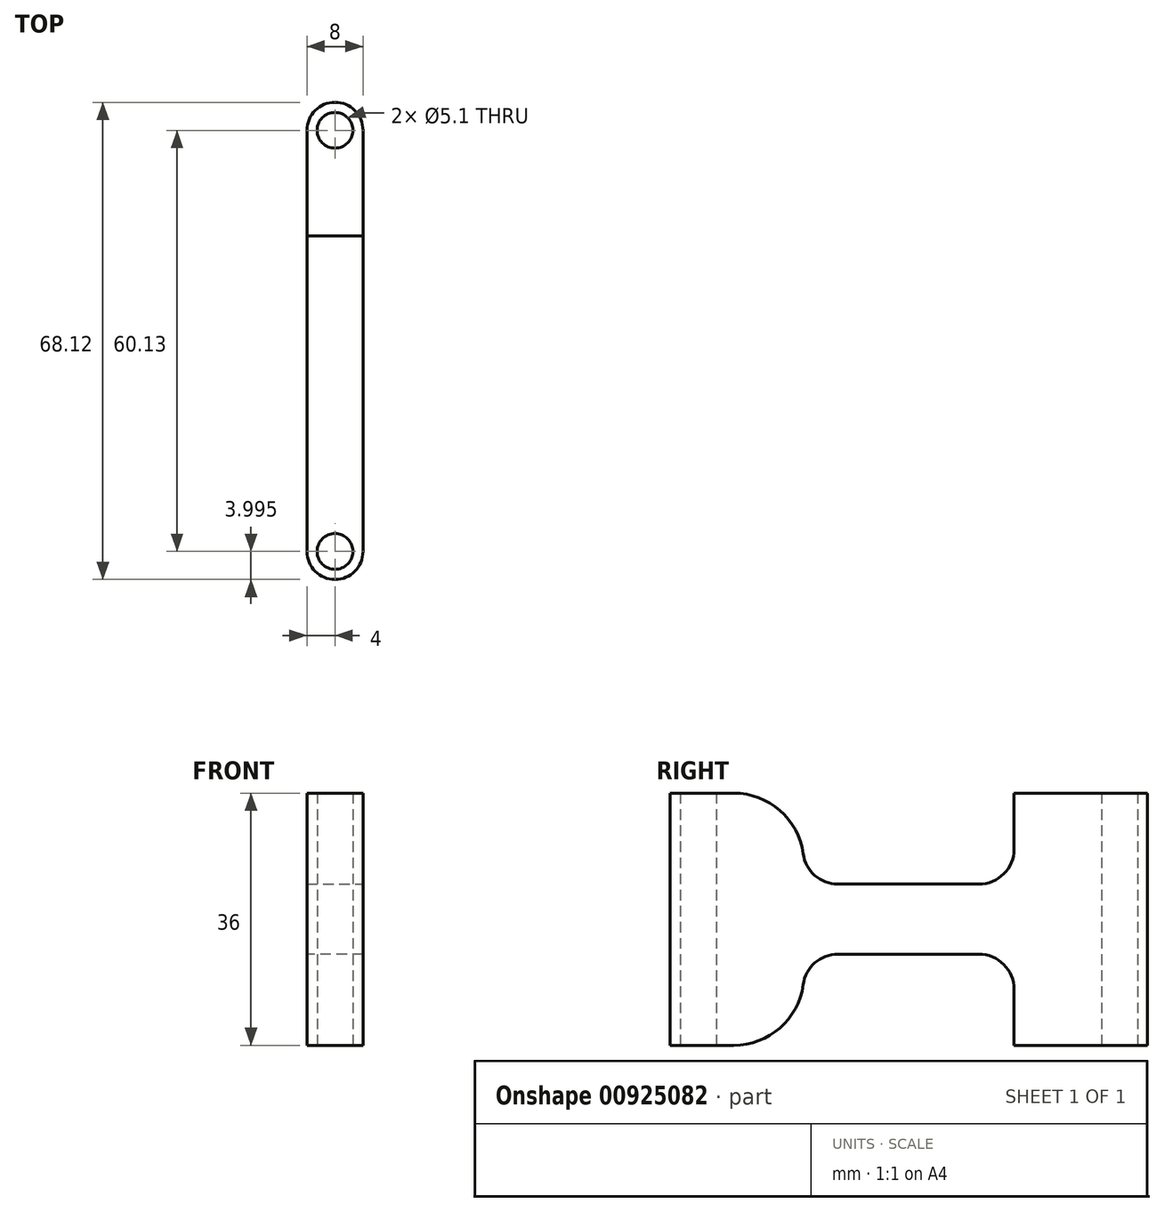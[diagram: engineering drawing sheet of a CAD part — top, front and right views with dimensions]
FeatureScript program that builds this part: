
annotation { "Feature Type Name" : "Feature", "Feature Type Description" : "" }
export const myFeature = defineFeature(function(context is Context, id is Id, definition is map)
    precondition{}
    {
        {
            var Q0;
            Q0=qCreatedBy(makeId("Top.planeOp"),FACE);
            var sketch = newSketch(context, id + "F0", { "sketchPlane" : qUnion([Q0])});
            skLineSegment(sketch, "E0.left", {"start": v(-4, 30.07) * mm, "end": v(-4, -30.07) * mm});
            skLineSegment(sketch, "E0.right", {"start": v(4, 30.07) * mm, "end": v(4, -30.07) * mm});
            skPoint(sketch, "E0.middle", {"position": v(0, 0) * mm});
            skCircle(sketch, "E1", {"center": v(0, -30.07) * mm, "radius": 2.55 * mm});
            skCircle(sketch, "E2", {"center": v(0, 30.07) * mm, "radius": 2.55 * mm});
            skArc(sketch, "E3", {"start": v(-4, -30.07) * mm, "mid": v(0, -34.07) * mm, "end": v(4, -30.07) * mm});
            skArc(sketch, "E4", {"start": v(4, 30.07) * mm, "mid": v(0, 34.06) * mm, "end": v(-4, 30.07) * mm});
            skSolve(sketch);
        }
        {
            var Q0;
            Q0=makeQuery(id+"F0.imprint","IMPRINT",FACE,{"disambiguationData":[TD([[makeQuery(id+"F0.imprint","IMPRINT",EDGE,{"derivedFrom":sQuery(id+"F0.wireOp",EDGE,"E0.left")}),1.0]])]});
            extrude(context, id + "F1", {"entities" : qUnion([Q0]), "depth" : 36 * mm, "offsetDistance" : 25 * mm});
        }
        {
            var Q0;
            Q0=makeQuery(id+"F1.opExtrude","SWEPT_FACE",FACE,{"disambiguationData":[OSD([sQuery(id+"F0.wireOp",EDGE,"E0.left")])]});
            var sketch = newSketch(context, id + "F2", { "sketchPlane" : qUnion([Q0])});
            skLineSegment(sketch, "E5", {"start": v(-30.07, 18) * mm, "end": v(30.07, 18) * mm, "construction": true});
            skLineSegment(sketch, "E6", {"start": v(0, 36) * mm, "end": v(0, 0) * mm, "construction": true});
            skLineSegment(sketch, "E7", {"start": v(0, 18) * mm, "end": v(0, 23) * mm, "construction": true});
            skLineSegment(sketch, "E8", {"start": v(0, 18) * mm, "end": v(0, 13) * mm, "construction": true});
            skLineSegment(sketch, "E9", {"start": v(0, 18) * mm, "end": v(-15, 18) * mm, "construction": true});
            skLineSegment(sketch, "E10", {"start": v(0, 18) * mm, "end": v(15, 18) * mm, "construction": true});
            skLineSegment(sketch, "E11", {"start": v(15, 18) * mm, "end": v(15, 23) * mm, "construction": true});
            skLineSegment(sketch, "E12", {"start": v(15, 23) * mm, "end": v(0, 23) * mm, "construction": true});
            skLineSegment(sketch, "E13", {"start": v(0, 23) * mm, "end": v(-15, 23) * mm, "construction": true});
            skLineSegment(sketch, "E14", {"start": v(-15, 23) * mm, "end": v(-15, 13) * mm, "construction": true});
            skLineSegment(sketch, "E15", {"start": v(-15, 13) * mm, "end": v(15, 13) * mm, "construction": true});
            skLineSegment(sketch, "E16", {"start": v(15, 13) * mm, "end": v(15, 18) * mm, "construction": true});
            skLineSegment(sketch, "E17", {"start": v(-15, 23) * mm, "end": v(-15, 36) * mm});
            skLineSegment(sketch, "E18", {"start": v(-15, 23) * mm, "end": v(15, 23) * mm});
            skLineSegment(sketch, "E19", {"start": v(15, 23) * mm, "end": v(15, 36) * mm});
            skLineSegment(sketch, "E20", {"start": v(15, 13) * mm, "end": v(15, 0) * mm});
            skLineSegment(sketch, "E21", {"start": v(15, 13) * mm, "end": v(-15, 13) * mm});
            skLineSegment(sketch, "E22", {"start": v(-15, 13) * mm, "end": v(-15, 0) * mm});
            skSolve(sketch);
        }
        {
            var Q0;
            {var subQ0=sQuery(id+"F2.wireOp",EDGE,"E17");Q0=makeQuery(id+"F2.imprint","IMPRINT",FACE,{"disambiguationData":[TD([[makeQuery(id+"F2.imprint","IMPRINT",EDGE,{"derivedFrom":subQ0}),-1.0]])]});}
            var Q1;
            {var subQ0=sQuery(id+"F2.wireOp",EDGE,"E20");Q1=makeQuery(id+"F2.imprint","IMPRINT",FACE,{"disambiguationData":[TD([[makeQuery(id+"F2.imprint","IMPRINT",EDGE,{"derivedFrom":subQ0}),-1.0]])]});}
            var Q2;
            Q2=makeQuery(id+"F1.opExtrude","SWEPT_FACE",FACE,{"disambiguationData":[OSD([sQuery(id+"F0.wireOp",EDGE,"E0.right")])]});
            extrude(context, id + "F3", {"entities" : qUnion([Q0, Q1]), "operationType" : NewBodyOperationType.REMOVE, "endBound" : BoundingType.UP_TO_SURFACE, "oppositeDirection" : true, "depth" : 25 * mm, "endBoundEntityFace" : qUnion([Q2]), "offsetDistance" : 25 * mm});
        }
        {
            var Q0;
            Q0=makeQuery(id+"F3.boolean.opBoolean","COPY",EDGE,{"derivedFrom":makeQuery(id+"F3.opExtrude","SWEPT_EDGE",EDGE,{"disambiguationData":[OSD([sQuery(id+"F0.wireOp",EDGE,"E0.left"),sQuery(id+"F2.wireOp",EDGE,"E17")])]})});
            var Q1;
            Q1=makeQuery(id+"F3.boolean.opBoolean","COPY",EDGE,{"derivedFrom":makeQuery(id+"F3.opExtrude","SWEPT_EDGE",EDGE,{"disambiguationData":[OSD([sQuery(id+"F0.wireOp",EDGE,"E0.left"),sQuery(id+"F2.wireOp",EDGE,"E22")])]})});
            var Q2;
            Q2=makeQuery(id+"F3.boolean.opBoolean","COPY",EDGE,{"derivedFrom":makeQuery(id+"F3.opExtrude","SWEPT_EDGE",EDGE,{"disambiguationData":[OSD([sQuery(id+"F0.wireOp",EDGE,"E0.left"),sQuery(id+"F2.wireOp",EDGE,"E20")])]})});
            var Q3;
            Q3=makeQuery(id+"F3.boolean.opBoolean","COPY",EDGE,{"derivedFrom":makeQuery(id+"F3.opExtrude","SWEPT_EDGE",EDGE,{"disambiguationData":[OSD([sQuery(id+"F0.wireOp",EDGE,"E0.left"),sQuery(id+"F2.wireOp",EDGE,"E19")])]})});
            fillet(context, id + "F4", {"entities" : qUnion([Q0, Q1, Q2, Q3]), "radius" : 10 * mm, "tangentPropagation" : true, "allowEdgeOverflow" : false});
        }
        {
            var Q0;
            Q0=makeQuery(id+"F3.boolean.opBoolean","COPY",EDGE,{"derivedFrom":makeQuery(id+"F3.opExtrude","SWEPT_EDGE",EDGE,{"disambiguationData":[OSD([sQuery(id+"F2.wireOp",EDGE,"E17"),sQuery(id+"F2.wireOp",EDGE,"E18")])]})});
            var Q1;
            Q1=makeQuery(id+"F3.boolean.opBoolean","COPY",EDGE,{"derivedFrom":makeQuery(id+"F3.opExtrude","SWEPT_EDGE",EDGE,{"disambiguationData":[OSD([sQuery(id+"F2.wireOp",EDGE,"E18"),sQuery(id+"F2.wireOp",EDGE,"E19")])]})});
            var Q2;
            Q2=makeQuery(id+"F3.boolean.opBoolean","COPY",EDGE,{"derivedFrom":makeQuery(id+"F3.opExtrude","SWEPT_EDGE",EDGE,{"disambiguationData":[OSD([sQuery(id+"F2.wireOp",EDGE,"E20"),sQuery(id+"F2.wireOp",EDGE,"E21")])]})});
            var Q3;
            Q3=makeQuery(id+"F3.boolean.opBoolean","COPY",EDGE,{"derivedFrom":makeQuery(id+"F3.opExtrude","SWEPT_EDGE",EDGE,{"disambiguationData":[OSD([sQuery(id+"F2.wireOp",EDGE,"E21"),sQuery(id+"F2.wireOp",EDGE,"E22")])]})});
            fillet(context, id + "F5", {"entities" : qUnion([Q0, Q1, Q2, Q3]), "radius" : 5 * mm, "tangentPropagation" : true, "allowEdgeOverflow" : false});
        }
    });
